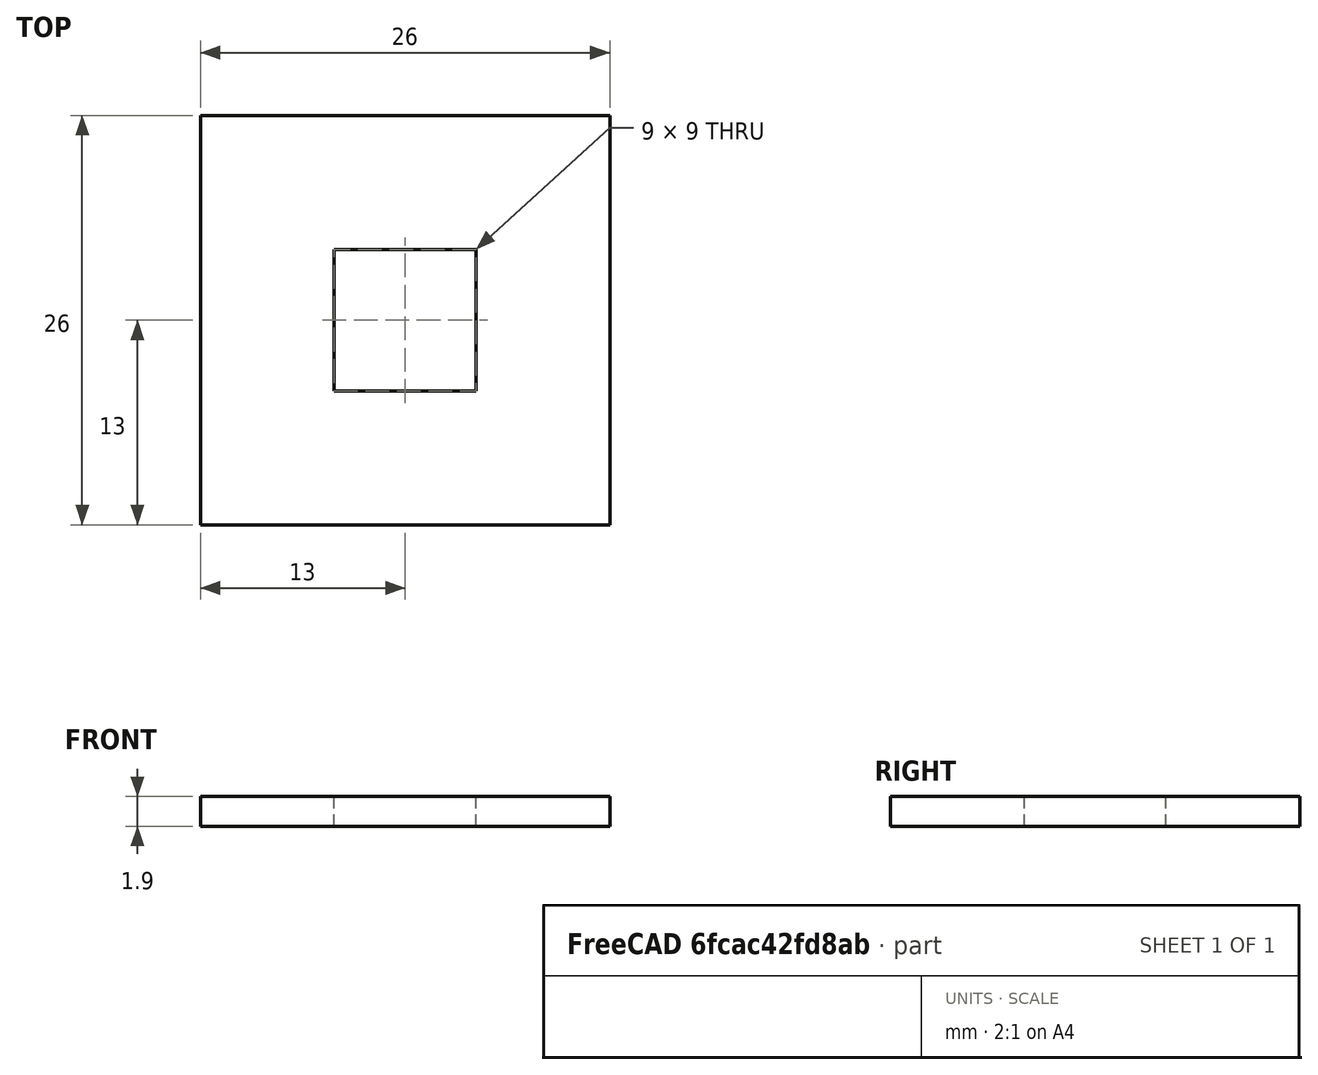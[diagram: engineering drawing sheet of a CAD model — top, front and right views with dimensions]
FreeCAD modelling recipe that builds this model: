
FCSTD DOCUMENT  (FreeCAD 2022.111R30764 (Git))
Label: square spacer
License: All rights reserved
LicenseURL: http://en.wikipedia.org/wiki/All_rights_reserved
objects: Sketcher::SketchObject×1, PartDesign::Pad×1, PartDesign::Body×1
note: 5 computed .brp shape members not serialized (recipe doc carries the construction recipe); baked Part::Feature solids carry a one-line shape summary decoded from their .brp

FEATURE [Sketcher::SketchObject] Sketch
  FullyConstrained = true
  MapMode = 5
  Support = -> [XY_Plane]
  TreeRank = 11
  sketch-geometry (10):
    g0: LineSegment StartX=-4.5 StartY=4.5 StartZ=0 EndX=-4.5 EndY=-4.5 EndZ=0
    g1: LineSegment StartX=-4.5 StartY=-4.5 StartZ=0 EndX=4.5 EndY=-4.5 EndZ=0
    g2: LineSegment StartX=4.5 StartY=-4.5 StartZ=0 EndX=4.5 EndY=4.5 EndZ=0
    g3: LineSegment StartX=4.5 StartY=4.5 StartZ=0 EndX=-4.5 EndY=4.5 EndZ=0
    g4: GeomPoint [constr] X=0 Y=0 Z=0
    g5: LineSegment StartX=-13 StartY=13 StartZ=0 EndX=-13 EndY=-13 EndZ=0
    g6: LineSegment StartX=-13 StartY=-13 StartZ=0 EndX=13 EndY=-13 EndZ=0
    g7: LineSegment StartX=13 StartY=-13 StartZ=0 EndX=13 EndY=13 EndZ=0
    g8: LineSegment StartX=13 StartY=13 StartZ=0 EndX=-13 EndY=13 EndZ=0
    g9: GeomPoint [constr] X=0 Y=0 Z=0
  constraints (24):
    c: Coincident(g0,g1)
    c: Coincident(g1,g2)
    c: Coincident(g2,g3)
    c: Coincident(g3,g0)
    c: Horizontal(g1)
    c: Horizontal(g3)
    c: Vertical(g0)
    c: Vertical(g2)
    c: Symmetric(g1,g0,g4)
    c: Coincident(g4,g-1)
    c: Coincident(g5,g6)
    c: Coincident(g6,g7)
    c: Coincident(g7,g8)
    c: Coincident(g8,g5)
    c: Horizontal(g6)
    c: Horizontal(g8)
    c: Vertical(g5)
    c: Vertical(g7)
    c: Symmetric(g6,g5,g9)
    c: Coincident(g9,g4)
    c: DistanceY(g7,g7) = 26
    c: DistanceX(g8,g8) = 26
    c: DistanceY(g2,g2) = 9
    c: DistanceX(g3,g3) = 9
FEATURE [PartDesign::Pad] Pad
  AddSubType = 0
  AlongSketchNormal = false
  CheckUpToFaceLimits = true
  ClaimChildren = false
  Direction = (0,0,1)
  Fit = 0
  FitJoin = 0
  InnerFit = 0
  InnerFitJoin = 0
  InnerTaperAngle = 0
  InnerTaperAngleRev = 0
  Length = 1.9
  Length2 = 100
  Linearize = true
  NewSolid = false
  Profile = -> Sketch
  Suppress = false
  TreeRank = 12
  Type = 0
  _ProfileBasedVersion = 1
FEATURE [PartDesign::Body] Body
  AutoGroupSolids = false
  ExportMode = 0
  Group = -> [Sketch,Pad]
  Origin = -> Origin
  Tip = -> Pad
  TreeRank = 10
  _ExportChildren = -> [Pad]
  _GroupVersion = 1
